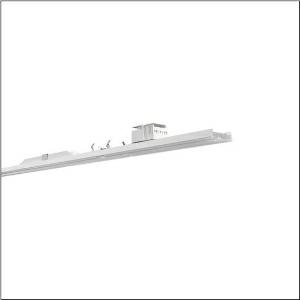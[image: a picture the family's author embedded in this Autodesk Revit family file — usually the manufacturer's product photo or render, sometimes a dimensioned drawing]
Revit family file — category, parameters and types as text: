
# Revit family: licross_r__11_recessed_mo_51tl18vn455f_736c
name_source: partatom
category: Lighting Fixtures
units: mm (PartAtom-declared; Revit-internal decimal feet)

## family parameters
Cut with Voids When Loaded = No
Host = Face
Light Source = No
Part Type = Normal
Room Calculation Point = No
Round Connector Dimension = Use Diameter
Shared = No

## types (1)
- --- (1 x LED, 5560 lm, 33.7 W, 4000K)
    Apparent Load = 34 VA
    CIE Flux Codes = 83 96 99 100 100
    Color Rendering = 80
    Color Temperature = 4000K
    Default Elevation = 1800 mm
    Description = Licross® 11 Recessed MOluminaire insert, length: 1.500mm, width: 66mm, height: 67mm, LED rated luminous flux: 5.560lm, light colour: 840, control gear: DALI 2, CLO, control gear: ECG DALI, with plug, 5-pole, with phase selection, mains connection: 220..240V, AC, 50/60Hz, halogen-free wiring, primary optical cover: cover, of PMMA, light emission: direct distribution, protection rating (complete): IP40, insulation class (complete): insulation class I (protective earthing), certification: CE, ENEC, VDE, UKCA, protection symbol: D if used in an environment without relevant dust loads with corresponding accessories, permissible ambient temperature for indoor applications: -25..+45°C, corresponds to IFS (International Featured Standards) requirements for safety and quality in the food industry, reducing of maximum allowable ambient temperature of 5°C with ceiling mounting, packaging unit: 1 piece
    Height = 58 mm
    Lamp = 1 x LED
    Lamp Light Flux = 5560 lm
    Lamp Power = 33.7 W
    Lamp count = 1
    Length = 1500 mm
    Luminous efficacy = 165 lm/W
    Manufacturer = Siteco
    ModVariant = No
    Model = 51TL18VN455F
    Mounting Place = Ceiling
    Mounting Type = Pendant
    Number of Poles = 1
    OnlyDefault = Yes
    Power Factor = 1
    Product Name = Licross® 11 Recessed MO
    Product group = luminaire insert
    ProductGroupID = 902
    Protection Class = Protection class I
    Protection Degree = IP 40
    RLX_Detail_Level = 1
    RlxData = <blob elided: 22413 chars, md5=f1ebd45b>
    Socket = socket
    Standby Power = 0 W
    System Light Flux = 5560 lm
    System Power = 34 W
    Type Comments = factory setting: luminous flux: 100 % | dim-lin: 254 | 221 mA
    Type Image = l_1266722.jpg
    URL = http://relux.com
    VarID = @adj_129029
    Voltage = 0 V
    Weight = 0.00 kg
    Width = 66 mm

## geometry (parser evidence)
native form markers: Blend x4, Sweep x10
no freeform markers — native parametric forms only
